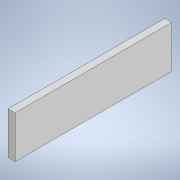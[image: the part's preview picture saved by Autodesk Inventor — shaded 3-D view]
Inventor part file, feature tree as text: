
AUTODESK INVENTOR PART (.ipt)
format: ipt  version: 2020 (Build 240168000, 168)  size: 90,624 bytes
history: native  units: mm
features: other x3, plane x1, extrude x1, sketch x1
ambient origin geometry x8: Origin, YZ Plane, XZ Plane, XY Plane, X Axis, Y Axis, Z Axis, Center Point
bodies: Solid1 (feature_tree)
feature tree (6):
  plane  "Work Plane1"
  extrude  "Extrusion1"  Depth=150.0mm
  sketch  "Sketch1"  dims[d0=25.0mm d1=150.0mm d2=556.0mm d3=0.0mm]
  parser-record x1  (decoder bookkeeping rows leaked as tree rows — omitted from the tree; the rows remain in map.json)
  other  "maquete.iam"
  other  "anteriorvertical:1"
note: 1 file-system path scrubbed to <path> (originals preserved in map.json)
